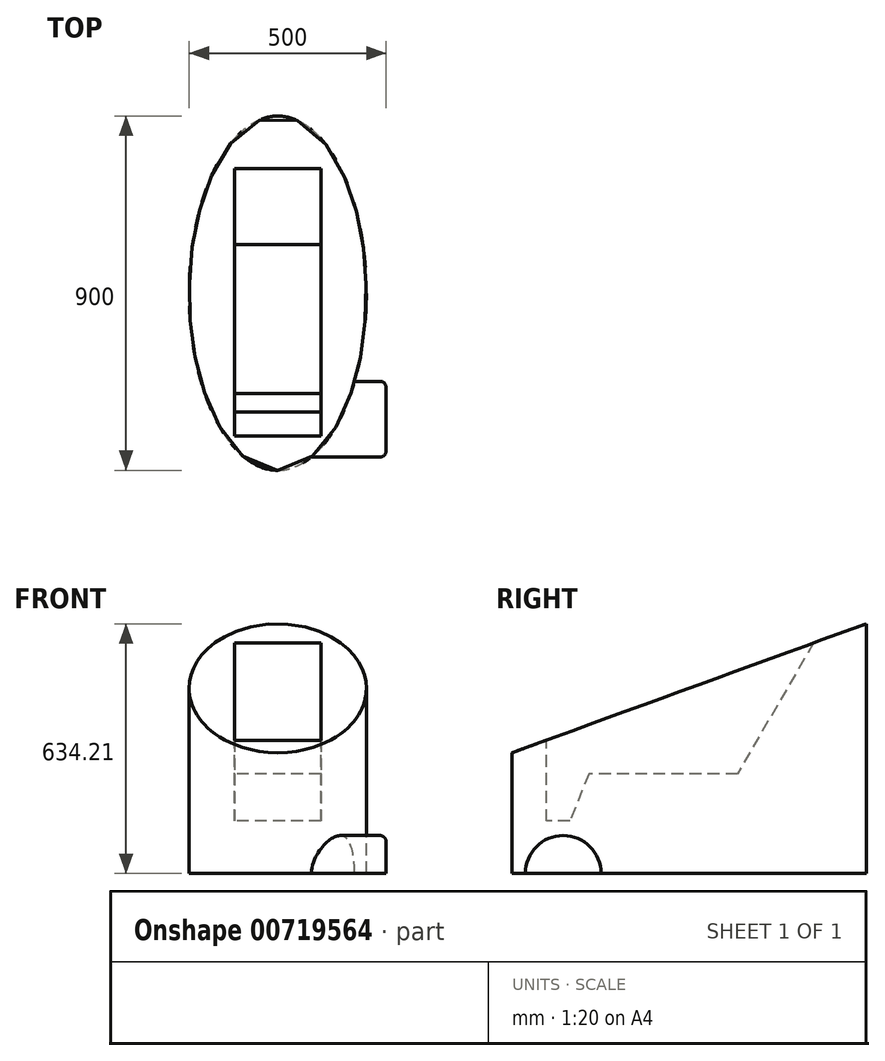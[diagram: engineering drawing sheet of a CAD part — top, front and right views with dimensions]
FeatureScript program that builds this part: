
annotation { "Feature Type Name" : "Feature", "Feature Type Description" : "" }
export const myFeature = defineFeature(function(context is Context, id is Id, definition is map)
    precondition{}
    {
        {
            var Q0;
            Q0=qCreatedBy(makeId("Top.planeOp"),FACE);
            var sketch = newSketch(context, id + "F0", { "sketchPlane" : qUnion([Q0])});
            skEllipse(sketch, "E0", {"center": v(0, 0) * mm, "majorRadius": 450 * mm, "minorRadius": 225 * mm, "majorAxis": v(0, -1)});
            skSolve(sketch);
        }
        {
            var Q0;
            Q0=makeQuery(id+"F0.imprint","IMPRINT",FACE,{"disambiguationData":[TD([[makeQuery(id+"F0.imprint","IMPRINT",EDGE,{"derivedFrom":sQuery(id+"F0.wireOp",EDGE,"E0")}),1.0]])]});
            extrude(context, id + "F1", {"entities" : qUnion([Q0]), "depth" : 700 * mm, "offsetDistance" : 25 * mm});
        }
        {
            var Q0;
            Q0=qCreatedBy(makeId("Right.planeOp"),FACE);
            var sketch = newSketch(context, id + "F2", { "sketchPlane" : qUnion([Q0])});
            skLineSegment(sketch, "E1", {"start": v(0, 0) * mm, "end": v(-329.33, 904.81) * mm, "construction": true});
            skLineSegment(sketch, "E2", {"start": v(0, 0) * mm, "end": v(0, 904.81) * mm, "construction": true});
            skLineSegment(sketch, "E3", {"start": v(484.63, 646.81) * mm, "end": v(-527.07, 278.59) * mm});
            skPoint(sketch, "E3.endSnap0", {"position": v(-164.66, 452.4) * mm});
            skLineSegment(sketch, "E4.0", {"start": v(-527.07, 278.59) * mm, "end": v(-705.2, 768) * mm});
            skPoint(sketch, "E5.orphan", {"position": v(-164.66, 410.49) * mm});
            skLineSegment(sketch, "E6", {"start": v(-705.2, 768) * mm, "end": v(306.5, 1136.23) * mm});
            skLineSegment(sketch, "E7", {"start": v(484.63, 646.81) * mm, "end": v(306.5, 1136.23) * mm});
            skSolve(sketch);
        }
        {
            var Q0;
            Q0=makeQuery(id+"F2.imprint","IMPRINT",FACE,{"disambiguationData":[TD([[makeQuery(id+"F2.imprint","IMPRINT",EDGE,{"derivedFrom":sQuery(id+"F2.wireOp",EDGE,"E3")}),-1.0]])]});
            extrude(context, id + "F3", {"entities" : qUnion([Q0]), "operationType" : NewBodyOperationType.REMOVE, "endBound" : BoundingType.SYMMETRIC, "oppositeDirection" : true, "depth" : 450 * mm, "offsetDistance" : 25 * mm});
        }
        {
            var Q0;
            Q0=qCreatedBy(makeId("Right.planeOp"),FACE);
            cPlane(context, id + "F4", {"entities" : qUnion([Q0]), "cplaneType" : CPlaneType.OFFSET, "offset" : 275 * mm, "width" : 150 * mm, "height" : 150 * mm});
        }
        {
            var Q0;
            Q0=qCreatedBy(id+"F4.planeOp",FACE);
            var sketch = newSketch(context, id + "F5", { "sketchPlane" : qUnion([Q0])});
            skArc(sketch, "E8", {"start": v(-223.8, 0) * mm, "mid": v(-320, 96.2) * mm, "end": v(-416.2, 0) * mm});
            skLineSegment(sketch, "E9", {"start": v(-416.2, 0) * mm, "end": v(-223.8, 0) * mm});
            skSolve(sketch);
        }
        {
            var Q0;
            Q0=makeQuery(id+"F5.imprint","IMPRINT",FACE,{"disambiguationData":[TD([[makeQuery(id+"F5.imprint","IMPRINT",EDGE,{"derivedFrom":sQuery(id+"F5.wireOp",EDGE,"E8")}),1.0]])]});
            var Q1;
            Q1=makeQuery(id+"F1.opExtrude","SWEPT_FACE",FACE,{"disambiguationData":[OSD([sQuery(id+"F0.wireOp",EDGE,"E0")])]});
            extrude(context, id + "F6", {"entities" : qUnion([Q0]), "endBound" : BoundingType.UP_TO_SURFACE, "oppositeDirection" : true, "depth" : 25 * mm, "endBoundEntityFace" : qUnion([Q1]), "offsetDistance" : 25 * mm});
        }
        {
            var Q0;
            Q0=makeQuery(id+"F6.opExtrude","CAP_EDGE",EDGE,{"disambiguationData":[OSD([sQuery(id+"F5.wireOp",EDGE,"E8")])],"isStart":true});
            fillet(context, id + "F7", {"entities" : qUnion([Q0]), "radius" : 15 * mm, "tangentPropagation" : true, "allowEdgeOverflow" : false});
        }
        {
            var Q0;
            Q0=qCreatedBy(makeId("Right.planeOp"),FACE);
            var sketch = newSketch(context, id + "F8", { "sketchPlane" : qUnion([Q0])});
            skLineSegment(sketch, "E10", {"start": v(348.14, 640.03) * mm, "end": v(123.1, 253.45) * mm});
            skLineSegment(sketch, "E11", {"start": v(123.1, 253.45) * mm, "end": v(-254.56, 253.45) * mm});
            skLineSegment(sketch, "E12", {"start": v(-362.63, 133.13) * mm, "end": v(-362.63, 437.27) * mm});
            skLineSegment(sketch, "E13", {"start": v(-362.63, 437.27) * mm, "end": v(348.14, 640.03) * mm});
            skLineSegment(sketch, "E14", {"start": v(-254.56, 253.45) * mm, "end": v(-302.47, 133.13) * mm});
            skLineSegment(sketch, "E15", {"start": v(-302.47, 133.13) * mm, "end": v(-362.63, 133.13) * mm});
            skSolve(sketch);
        }
        {
            var Q0;
            Q0=makeQuery(id+"F8.imprint","IMPRINT",FACE,{"disambiguationData":[TD([[makeQuery(id+"F8.imprint","IMPRINT",EDGE,{"derivedFrom":sQuery(id+"F8.wireOp",EDGE,"E10")}),-1.0]])]});
            extrude(context, id + "F9", {"entities" : qUnion([Q0]), "operationType" : NewBodyOperationType.REMOVE, "endBound" : BoundingType.SYMMETRIC, "depth" : 220 * mm, "offsetDistance" : 25 * mm});
        }
    });
